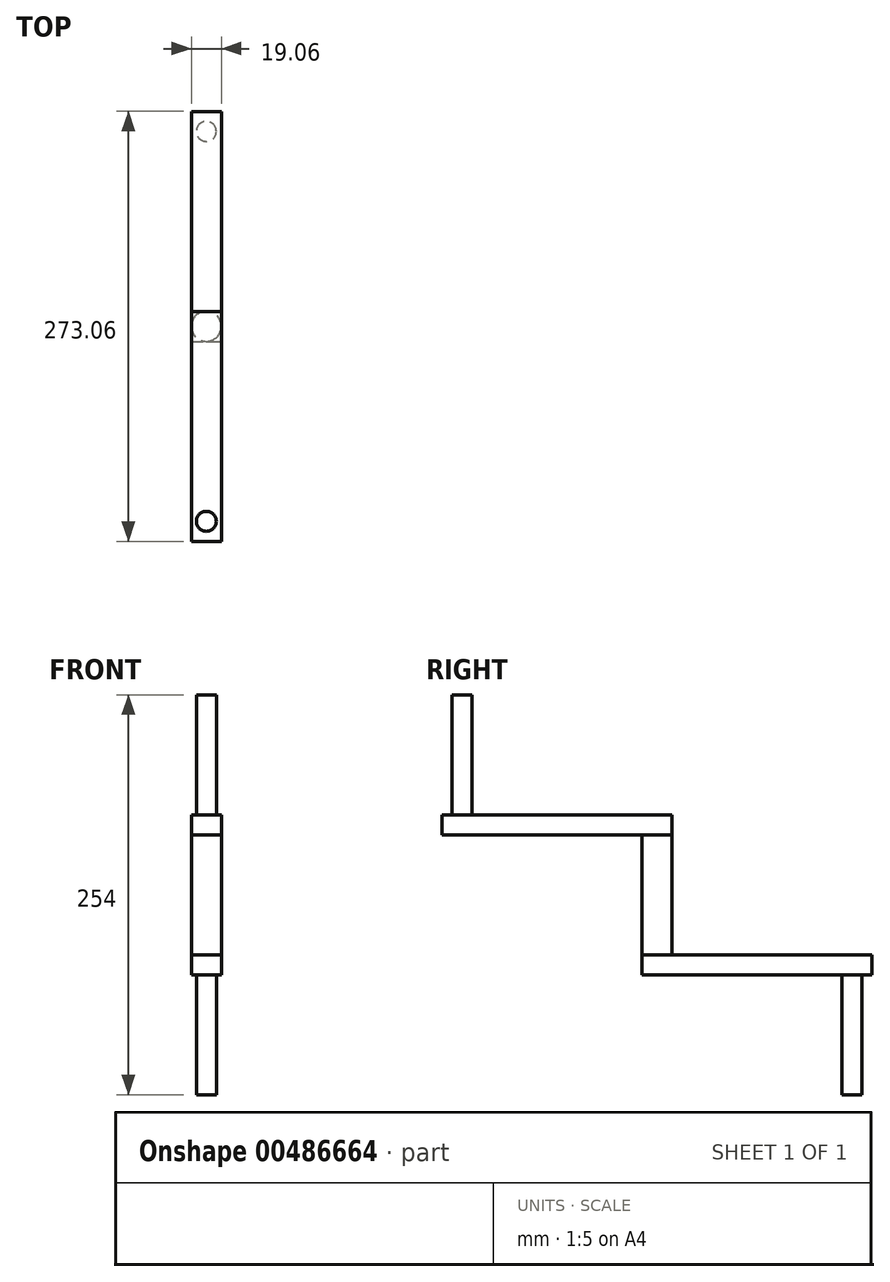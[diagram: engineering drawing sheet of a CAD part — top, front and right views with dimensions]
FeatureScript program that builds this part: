
annotation { "Feature Type Name" : "Feature", "Feature Type Description" : "" }
export const myFeature = defineFeature(function(context is Context, id is Id, definition is map)
    precondition{}
    {
        {
            var Q0;
            Q0=qCreatedBy(makeId("Top.planeOp"),FACE);
            var sketch = newSketch(context, id + "F0", { "sketchPlane" : qUnion([Q0])});
            skCircle(sketch, "E0", {"center": v(0, 0) * mm, "radius": 9.53 * mm});
            skSolve(sketch);
        }
        {
            var Q0;
            Q0 = qSketchRegion(id + "F0", true);
            extrude(context, id + "F1", {"entities" : qUnion([Q0]), "endBound" : BoundingType.SYMMETRIC, "depth" : 76.2 * mm, "offsetDistance" : 25.4 * mm});
        }
        {
            var Q0;
            Q0=makeQuery(id+"F1.opExtrude","CAP_FACE",FACE,{"disambiguationData":[OSD([sQuery(id+"F0.wireOp",EDGE,"E0")])],"isStart":false});
            var sketch = newSketch(context, id + "F2", { "sketchPlane" : qUnion([Q0])});
            skLineSegment(sketch, "E1.bottom", {"start": v(-9.53, 9.53) * mm, "end": v(9.53, 9.53) * mm});
            skLineSegment(sketch, "E1.top", {"start": v(-9.53, -9.53) * mm, "end": v(9.53, -9.53) * mm});
            skLineSegment(sketch, "E1.left", {"start": v(-9.53, 9.53) * mm, "end": v(-9.53, -9.53) * mm});
            skLineSegment(sketch, "E1.right", {"start": v(9.53, 9.53) * mm, "end": v(9.53, -9.52) * mm});
            skPoint(sketch, "E1.middle", {"position": v(0, 0) * mm});
            skSolve(sketch);
        }
        {
            var Q0;
            Q0 = qSketchRegion(id + "F2", true);
            extrude(context, id + "F3", {"entities" : qUnion([Q0]), "operationType" : NewBodyOperationType.ADD, "depth" : 12.7 * mm, "offsetDistance" : 25.4 * mm});
        }
        {
            var Q0;
            Q0=makeQuery(id+"F3.opExtrude","SWEPT_FACE",FACE,{"disambiguationData":[OSD([sQuery(id+"F2.wireOp",EDGE,"E1.top")])]});
            var sketch = newSketch(context, id + "F4", { "sketchPlane" : qUnion([Q0])});
            skLineSegment(sketch, "E2.bottom", {"start": v(-9.53, 50.8) * mm, "end": v(9.53, 50.8) * mm});
            skLineSegment(sketch, "E2.top", {"start": v(-9.53, 38.1) * mm, "end": v(9.53, 38.1) * mm});
            skLineSegment(sketch, "E2.left", {"start": v(-9.53, 50.8) * mm, "end": v(-9.53, 38.1) * mm});
            skLineSegment(sketch, "E2.right", {"start": v(9.53, 50.8) * mm, "end": v(9.53, 38.1) * mm});
            skSolve(sketch);
        }
        {
            var Q0;
            Q0 = qSketchRegion(id + "F4", true);
            extrude(context, id + "F5", {"entities" : qUnion([Q0]), "operationType" : NewBodyOperationType.ADD, "depth" : 127 * mm, "offsetDistance" : 25.4 * mm});
        }
        {
            var Q0;
            Q0=makeQuery(id+"F1.opExtrude","CAP_FACE",FACE,{"disambiguationData":[OSD([sQuery(id+"F0.wireOp",EDGE,"E0")])],"isStart":true});
            var sketch = newSketch(context, id + "F6", { "sketchPlane" : qUnion([Q0])});
            skLineSegment(sketch, "E3.bottom", {"start": v(-9.53, 9.53) * mm, "end": v(9.52, 9.53) * mm});
            skLineSegment(sketch, "E3.top", {"start": v(-9.53, -9.53) * mm, "end": v(9.52, -9.53) * mm});
            skLineSegment(sketch, "E3.left", {"start": v(-9.53, 9.52) * mm, "end": v(-9.53, -9.53) * mm});
            skLineSegment(sketch, "E3.right", {"start": v(9.52, 9.53) * mm, "end": v(9.52, -9.52) * mm});
            skPoint(sketch, "E3.middle", {"position": v(0, 0) * mm});
            skSolve(sketch);
        }
        {
            var Q0;
            Q0 = qSketchRegion(id + "F6", true);
            extrude(context, id + "F7", {"entities" : qUnion([Q0]), "operationType" : NewBodyOperationType.ADD, "depth" : 12.7 * mm, "offsetDistance" : 25.4 * mm});
        }
        {
            var Q0;
            Q0=makeQuery(id+"F7.opExtrude","SWEPT_FACE",FACE,{"disambiguationData":[OSD([sQuery(id+"F6.wireOp",EDGE,"E3.top")])]});
            var sketch = newSketch(context, id + "F8", { "sketchPlane" : qUnion([Q0])});
            skLineSegment(sketch, "E4.bottom", {"start": v(-9.52, -38.1) * mm, "end": v(9.53, -38.1) * mm});
            skLineSegment(sketch, "E4.top", {"start": v(-9.52, -50.8) * mm, "end": v(9.53, -50.8) * mm});
            skLineSegment(sketch, "E4.left", {"start": v(-9.52, -38.1) * mm, "end": v(-9.52, -50.8) * mm});
            skLineSegment(sketch, "E4.right", {"start": v(9.53, -38.1) * mm, "end": v(9.53, -50.8) * mm});
            skSolve(sketch);
        }
        {
            var Q0;
            Q0 = qSketchRegion(id + "F8", true);
            extrude(context, id + "F9", {"entities" : qUnion([Q0]), "operationType" : NewBodyOperationType.ADD, "depth" : 127 * mm, "offsetDistance" : 25.4 * mm});
        }
        {
            var Q0;
            Q0=makeQuery(id+"F5.boolean.opBoolean","MERGE",FACE,{"derivedFrom":[makeQuery(id+"F3.opExtrude","CAP_FACE",FACE,{"disambiguationData":[OSD([sQuery(id+"F2.wireOp",EDGE,"E1.bottom"),sQuery(id+"F2.wireOp",EDGE,"E1.top"),sQuery(id+"F2.wireOp",EDGE,"E1.left"),sQuery(id+"F2.wireOp",EDGE,"E1.right")])],"isStart":false}),makeQuery(id+"F5.opExtrude","SWEPT_FACE",FACE,{"disambiguationData":[OSD([sQuery(id+"F4.wireOp",EDGE,"E2.bottom")])]})]});
            var sketch = newSketch(context, id + "F10", { "sketchPlane" : qUnion([Q0])});
            skCircle(sketch, "E5", {"center": v(0, -123.83) * mm, "radius": 6.35 * mm});
            skSolve(sketch);
        }
        {
            var Q0;
            Q0 = qSketchRegion(id + "F10", true);
            extrude(context, id + "F11", {"entities" : qUnion([Q0]), "operationType" : NewBodyOperationType.ADD, "depth" : 76.2 * mm, "offsetDistance" : 25.4 * mm});
        }
        {
            var Q0;
            Q0=makeQuery(id+"F9.boolean.opBoolean","MERGE",FACE,{"derivedFrom":[makeQuery(id+"F7.opExtrude","CAP_FACE",FACE,{"disambiguationData":[OSD([sQuery(id+"F6.wireOp",EDGE,"E3.bottom"),sQuery(id+"F6.wireOp",EDGE,"E3.top"),sQuery(id+"F6.wireOp",EDGE,"E3.left"),sQuery(id+"F6.wireOp",EDGE,"E3.right")])],"isStart":false}),makeQuery(id+"F9.opExtrude","SWEPT_FACE",FACE,{"disambiguationData":[OSD([sQuery(id+"F8.wireOp",EDGE,"E4.top")])]})]});
            var sketch = newSketch(context, id + "F12", { "sketchPlane" : qUnion([Q0])});
            skCircle(sketch, "E6", {"center": v(0, -123.83) * mm, "radius": 6.35 * mm});
            skSolve(sketch);
        }
        {
            var Q0;
            Q0 = qSketchRegion(id + "F12", true);
            extrude(context, id + "F13", {"entities" : qUnion([Q0]), "operationType" : NewBodyOperationType.ADD, "depth" : 76.2 * mm, "offsetDistance" : 25.4 * mm});
        }
    });
